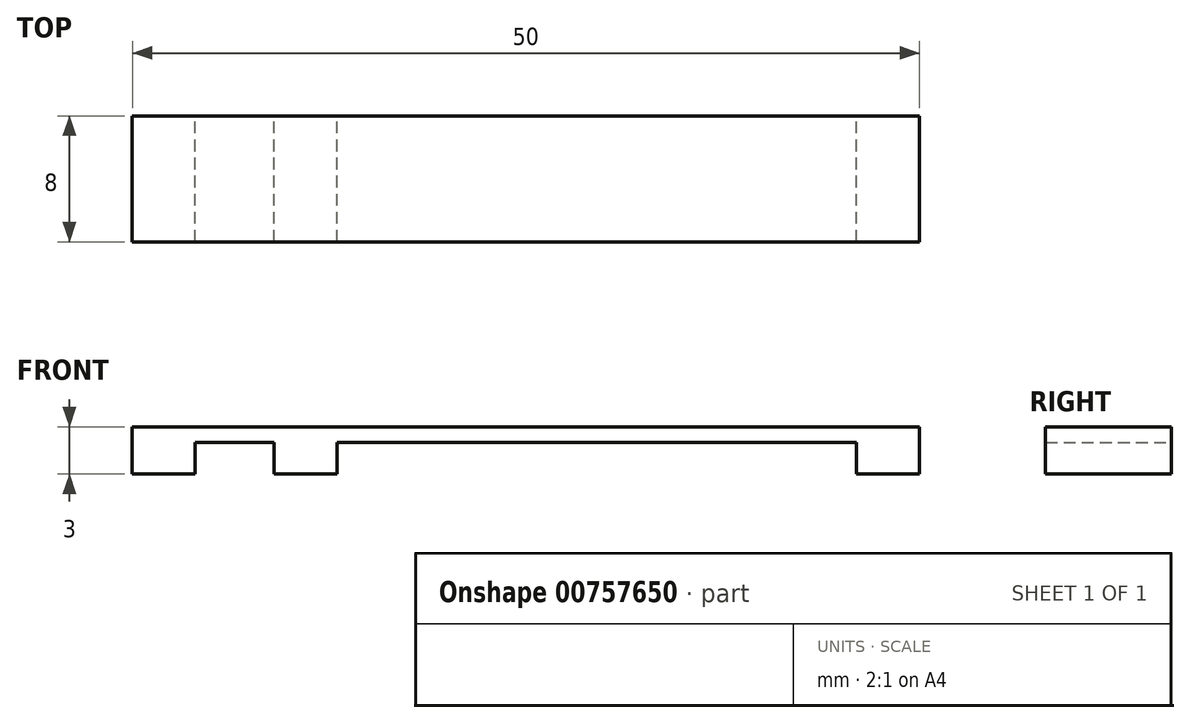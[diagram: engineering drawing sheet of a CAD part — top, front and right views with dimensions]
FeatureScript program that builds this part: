
annotation { "Feature Type Name" : "Feature", "Feature Type Description" : "" }
export const myFeature = defineFeature(function(context is Context, id is Id, definition is map)
    precondition{}
    {
        {
            var Q0;
            Q0=qCreatedBy(makeId("Front.planeOp"),FACE);
            var sketch = newSketch(context, id + "F0", { "sketchPlane" : qUnion([Q0])});
            skLineSegment(sketch, "E0.bottom", {"start": v(-36.6, 1) * mm, "end": v(13.4, 1) * mm});
            skLineSegment(sketch, "E0.top", {"start": v(-36.6, -2) * mm, "end": v(-32.6, -2) * mm});
            skLineSegment(sketch, "E0.left", {"start": v(-36.6, 1) * mm, "end": v(-36.6, -2) * mm});
            skLineSegment(sketch, "E0.right", {"start": v(13.4, 1) * mm, "end": v(13.4, -2) * mm});
            skLineSegment(sketch, "E1.top", {"start": v(-32.6, 0) * mm, "end": v(-27.6, 0) * mm});
            skLineSegment(sketch, "E1.left", {"start": v(-32.6, -2) * mm, "end": v(-32.6, 0) * mm});
            skLineSegment(sketch, "E1.right", {"start": v(9.4, -2) * mm, "end": v(9.4, 0) * mm});
            skLineSegment(sketch, "E2.trimOffspring", {"start": v(9.4, -2) * mm, "end": v(13.4, -2) * mm});
            skLineSegment(sketch, "E3", {"start": v(-27.6, 0) * mm, "end": v(-27.6, -2) * mm});
            skLineSegment(sketch, "E4", {"start": v(-27.6, -2) * mm, "end": v(-23.6, -2) * mm});
            skLineSegment(sketch, "E5", {"start": v(-23.6, -2) * mm, "end": v(-23.6, 0) * mm});
            skLineSegment(sketch, "E6.trimOffspring", {"start": v(-23.6, 0) * mm, "end": v(9.4, 0) * mm});
            skSolve(sketch);
        }
        {
            var Q0;
            Q0 = qSketchRegion(id + "F0", true);
            extrude(context, id + "F1", {"entities" : qUnion([Q0]), "endBound" : BoundingType.SYMMETRIC, "depth" : 8 * mm, "offsetDistance" : 25 * mm});
        }
    });
